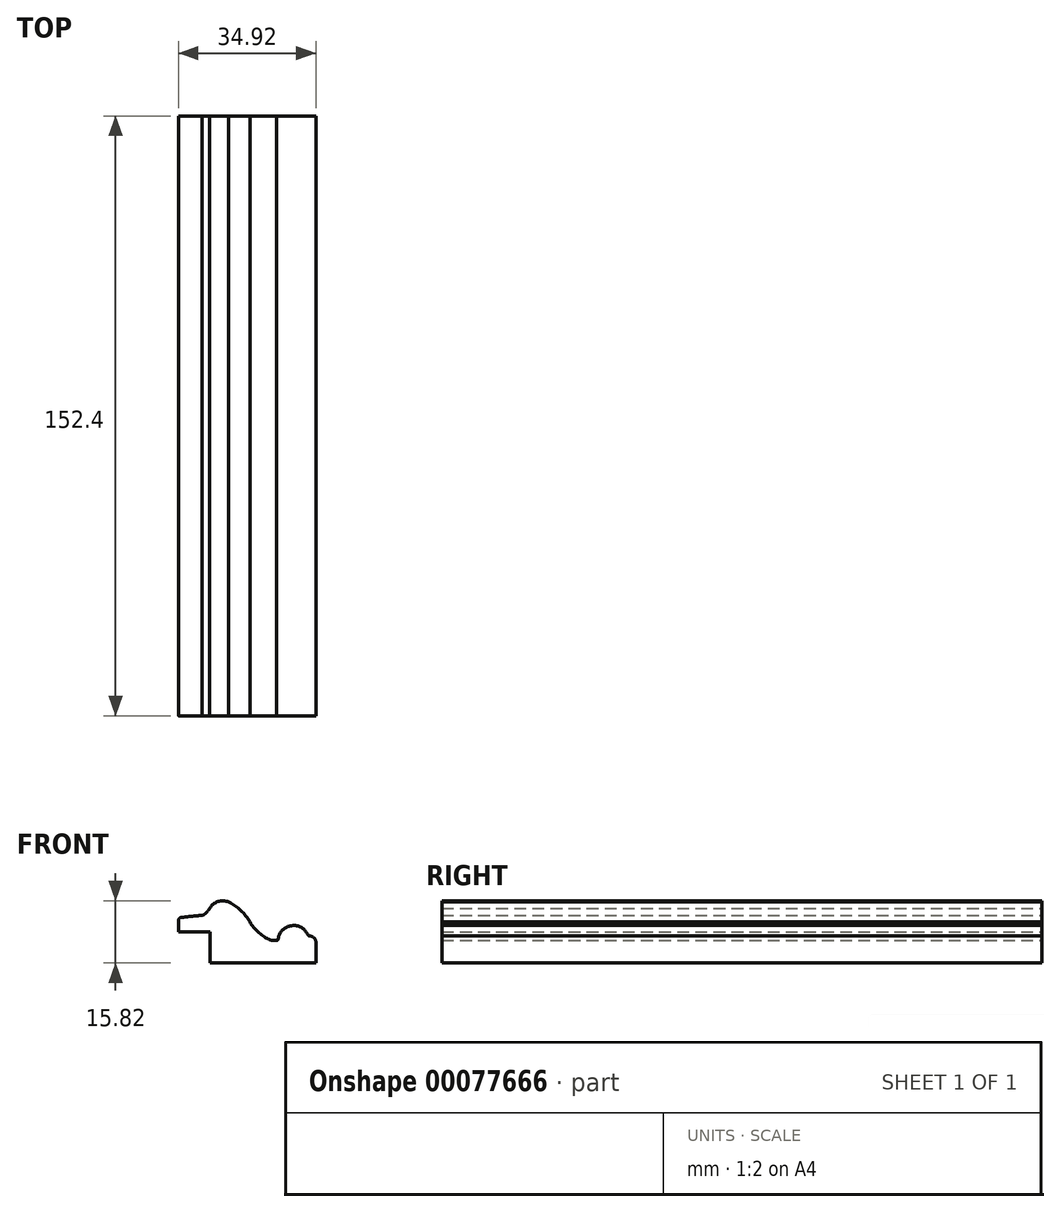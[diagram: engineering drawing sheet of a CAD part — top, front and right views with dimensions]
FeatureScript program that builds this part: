
annotation { "Feature Type Name" : "Feature", "Feature Type Description" : "" }
export const myFeature = defineFeature(function(context is Context, id is Id, definition is map)
    precondition{}
    {
        {
            var Q0;
            Q0=qCreatedBy(makeId("Front.planeOp"),FACE);
            var sketch = newSketch(context, id + "F0", { "sketchPlane" : qUnion([Q0])});
            skLineSegment(sketch, "E0", {"start": v(-9.46, -7.9) * mm, "end": v(-9.46, 0.03) * mm});
            skLineSegment(sketch, "E1", {"start": v(-17.46, 0.03) * mm, "end": v(-9.46, 0.03) * mm});
            skLineSegment(sketch, "E2", {"start": v(6.6, -2.16) * mm, "end": v(7.49, -2.16) * mm});
            skArc(sketch, "E3", {"start": v(15.45, -0.8) * mm, "mid": v(11.27, 1.6) * mm, "end": v(7.86, -1.82) * mm});
            skArc(sketch, "E4", {"start": v(7.48, -2.16) * mm, "mid": v(7.73, -2.06) * mm, "end": v(7.86, -1.82) * mm});
            skLineSegment(sketch, "E5", {"start": v(17.46, -2.66) * mm, "end": v(17.46, -7.9) * mm});
            skLineSegment(sketch, "E6", {"start": v(-17.46, 2.9) * mm, "end": v(-17.46, 0.03) * mm});
            skArc(sketch, "E7", {"start": v(17.46, -2.66) * mm, "mid": v(16.98, -1.5) * mm, "end": v(15.8, -1.04) * mm});
            skArc(sketch, "E8", {"start": v(15.45, -0.8) * mm, "mid": v(15.6, -0.98) * mm, "end": v(15.8, -1.04) * mm});
            skArc(sketch, "E9", {"start": v(-4.68, 7.59) * mm, "mid": v(-7.44, 7.7) * mm, "end": v(-9.55, 5.94) * mm});
            skArc(sketch, "E10", {"start": v(-10.72, 4.55) * mm, "mid": v(-10.09, 5.21) * mm, "end": v(-9.55, 5.94) * mm});
            skArc(sketch, "E11", {"start": v(-11.52, 4.23) * mm, "mid": v(-14.16, 3.96) * mm, "end": v(-16.79, 3.66) * mm});
            skArc(sketch, "E12", {"start": v(-16.79, 3.66) * mm, "mid": v(-17.27, 3.41) * mm, "end": v(-17.46, 2.9) * mm});
            skArc(sketch, "E13", {"start": v(-11.52, 4.23) * mm, "mid": v(-11.1, 4.32) * mm, "end": v(-10.72, 4.55) * mm});
            skArc(sketch, "E14", {"start": v(0.68, 2.5) * mm, "mid": v(-1.62, 5.44) * mm, "end": v(-4.68, 7.59) * mm});
            skArc(sketch, "E15", {"start": v(0.68, 2.5) * mm, "mid": v(2.77, 0.01) * mm, "end": v(5.41, -1.86) * mm});
            skArc(sketch, "E16", {"start": v(5.41, -1.86) * mm, "mid": v(6, -2.08) * mm, "end": v(6.6, -2.16) * mm});
            skLineSegment(sketch, "E17", {"start": v(-9.46, 0.03) * mm, "end": v(-17.46, 0.03) * mm});
            skLineSegment(sketch, "E18", {"start": v(17.46, -7.9) * mm, "end": v(-9.46, -7.9) * mm});
            skSolve(sketch);
        }
        {
            var Q0;
            {var subQ0=sQuery(id+"F0.wireOp",EDGE,"E2");Q0=makeQuery(id+"F0.imprint","IMPRINT",FACE,{"disambiguationData":[TD([[makeQuery(id+"F0.imprint","IMPRINT",EDGE,{"derivedFrom":subQ0}),-1.0]])]});}
            extrude(context, id + "F1", {"entities" : qUnion([Q0]), "depth" : 152.4 * mm});
        }
    });
